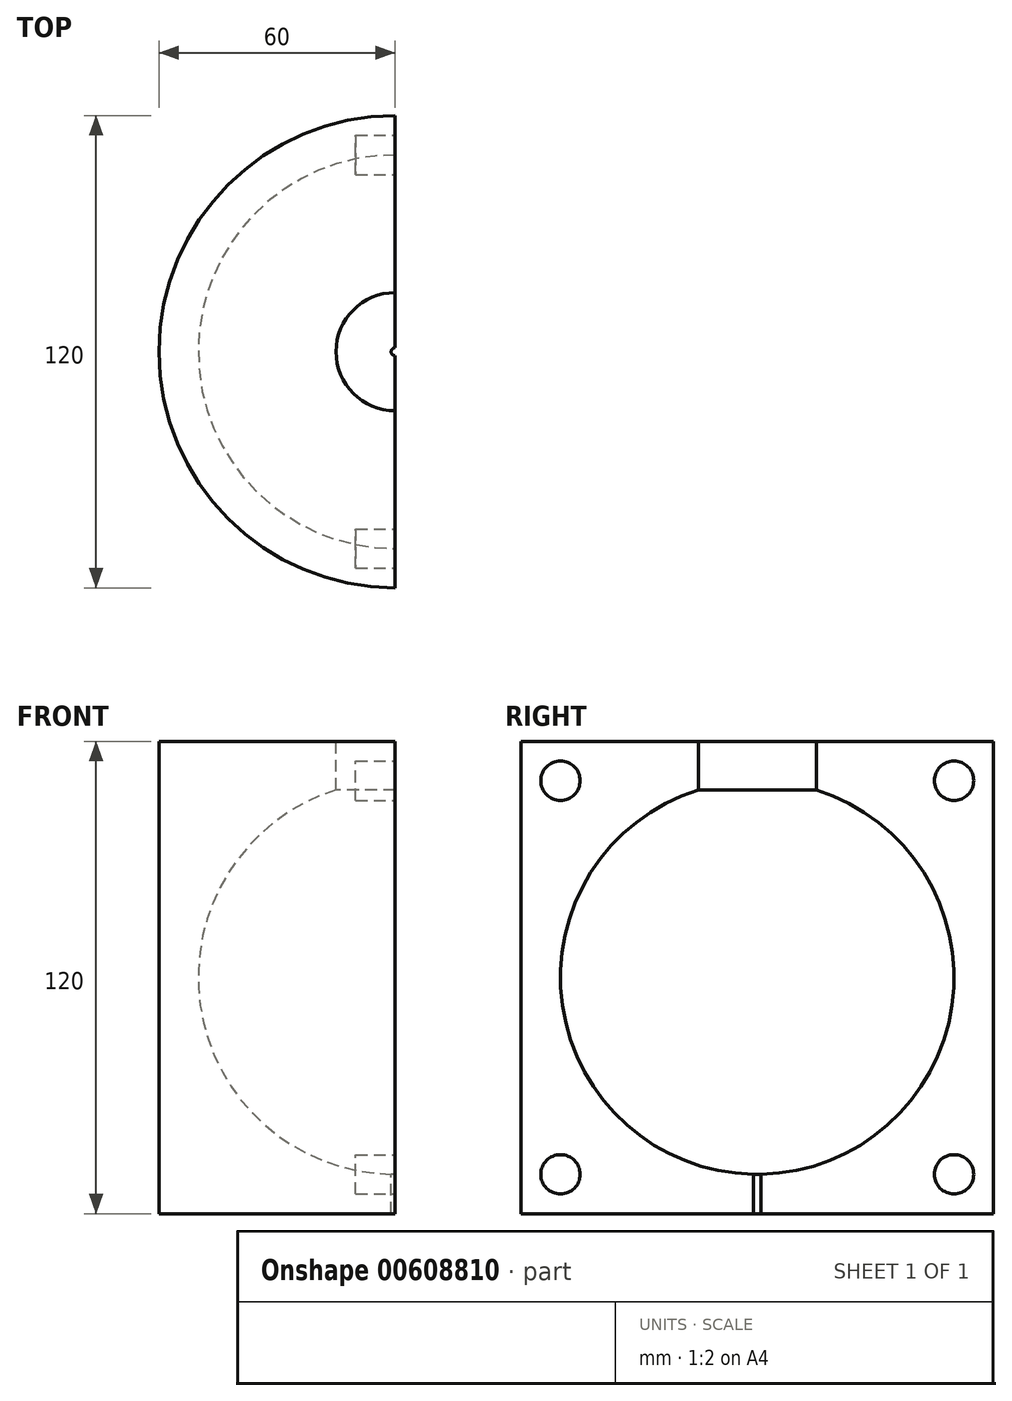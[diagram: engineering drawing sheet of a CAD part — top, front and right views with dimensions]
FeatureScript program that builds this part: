
annotation { "Feature Type Name" : "Feature", "Feature Type Description" : "" }
export const myFeature = defineFeature(function(context is Context, id is Id, definition is map)
    precondition{}
    {
        {
            var Q0;
            Q0=qCreatedBy(makeId("Right.planeOp"),FACE);
            var sketch = newSketch(context, id + "F0", { "sketchPlane" : qUnion([Q0])});
            skLineSegment(sketch, "E0", {"start": v(6.46, -45.64) * mm, "end": v(6.46, 64.36) * mm, "construction": true});
            skLineSegment(sketch, "E1", {"start": v(6.46, 64.36) * mm, "end": v(-8.54, 64.36) * mm, "construction": true});
            skLineSegment(sketch, "E2", {"start": v(-8.54, 64.36) * mm, "end": v(-53.54, 64.36) * mm});
            skLineSegment(sketch, "E3", {"start": v(-53.54, 64.36) * mm, "end": v(-53.54, -55.64) * mm});
            skLineSegment(sketch, "E4", {"start": v(-53.54, -55.64) * mm, "end": v(5.46, -55.64) * mm});
            skLineSegment(sketch, "E5", {"start": v(-8.54, 64.36) * mm, "end": v(-8.54, 54.36) * mm});
            skPoint(sketch, "E6", {"position": v(6.46, 4.36) * mm});
            skLineSegment(sketch, "E7", {"start": v(-8.54, 54.36) * mm, "end": v(-8.54, 52.06) * mm});
            skPoint(sketch, "E8", {"position": v(-43.54, 4.36) * mm});
            skPoint(sketch, "E9", {"position": v(6.46, -45.64) * mm});
            skPoint(sketch, "E10", {"position": v(-8.54, -45.64) * mm});
            skLineSegment(sketch, "E11", {"start": v(-8.54, -45.64) * mm, "end": v(5.46, -45.64) * mm});
            skPoint(sketch, "E12.orphan", {"position": v(-8.54, -55.64) * mm});
            skPoint(sketch, "E13", {"position": v(-43.54, 54.36) * mm});
            skLineSegment(sketch, "E14", {"start": v(-43.54, 4.36) * mm, "end": v(-43.54, 4.36) * mm});
            skArc(sketch, "E15.filletArc", {"start": v(-8.54, 52.06) * mm, "mid": v(-33.85, 33.94) * mm, "end": v(-43.54, 4.36) * mm});
            skPoint(sketch, "E16.visualSharp", {"position": v(-43.54, -45.64) * mm});
            skArc(sketch, "E16.filletArc", {"start": v(-43.54, 4.36) * mm, "mid": v(-28.9, -31) * mm, "end": v(6.46, -45.64) * mm});
            skLineSegment(sketch, "E17", {"start": v(5.46, -45.64) * mm, "end": v(5.46, -55.64) * mm});
            skPoint(sketch, "E18.orphan", {"position": v(6.46, -55.64) * mm});
            skLineSegment(sketch, "E19", {"start": v(5.46, -45.64) * mm, "end": v(5.46, -45.6) * mm});
            skLineSegment(sketch, "E20.MirrorCS", {"start": v(66.46, -55.64) * mm, "end": v(7.46, -55.64) * mm});
            skLineSegment(sketch, "E21.MirrorCS", {"start": v(66.46, 64.36) * mm, "end": v(66.46, -55.64) * mm});
            skLineSegment(sketch, "E22.MirrorCS", {"start": v(21.46, 64.36) * mm, "end": v(66.46, 64.36) * mm});
            skLineSegment(sketch, "E23.MirrorCS", {"start": v(21.46, 64.36) * mm, "end": v(21.46, 54.36) * mm});
            skLineSegment(sketch, "E24.MirrorCS", {"start": v(21.46, 54.36) * mm, "end": v(21.46, 52.06) * mm});
            skArc(sketch, "E25.MirrorCS", {"start": v(21.46, 52.06) * mm, "mid": v(46.77, 33.94) * mm, "end": v(56.46, 4.36) * mm});
            skArc(sketch, "E26.MirrorCS", {"start": v(56.46, 4.36) * mm, "mid": v(41.82, -31) * mm, "end": v(6.46, -45.64) * mm});
            skLineSegment(sketch, "E27.MirrorCS", {"start": v(7.46, -45.64) * mm, "end": v(7.46, -55.64) * mm});
            skLineSegment(sketch, "E28.MirrorCS", {"start": v(7.46, -45.64) * mm, "end": v(7.46, -45.6) * mm});
            skPoint(sketch, "E29.MirrorP", {"position": v(56.46, -45.64) * mm});
            skPoint(sketch, "E30.MirrorP", {"position": v(56.46, 54.36) * mm});
            skCircle(sketch, "E31", {"center": v(-43.54, -45.64) * mm, "radius": 5 * mm});
            skCircle(sketch, "E32", {"center": v(-43.54, 54.36) * mm, "radius": 5 * mm});
            skCircle(sketch, "E33", {"center": v(56.46, -45.64) * mm, "radius": 5 * mm});
            skCircle(sketch, "E34", {"center": v(56.46, 54.36) * mm, "radius": 5 * mm});
            skSolve(sketch);
        }
        {
            var Q0;
            Q0=makeQuery(id+"F0.imprint","IMPRINT",FACE,{"disambiguationData":[TD([[makeQuery(id+"F0.imprint","IMPRINT",EDGE,{"derivedFrom":sQuery(id+"F0.wireOp",EDGE,"E2")}),1.0]])]});
            var Q1;
            Q1=makeQuery(id+"F0.imprint","IMPRINT",FACE,{"disambiguationData":[TD([[makeQuery(id+"F0.imprint","IMPRINT",EDGE,{"derivedFrom":sQuery(id+"F0.wireOp",EDGE,"E32")}),1.0]])]});
            var Q2;
            Q2=makeQuery(id+"F0.imprint","IMPRINT",FACE,{"disambiguationData":[TD([[makeQuery(id+"F0.imprint","IMPRINT",EDGE,{"derivedFrom":sQuery(id+"F0.wireOp",EDGE,"E31")}),1.0]])]});
            var Q3;
            Q3=sQuery(id+"F0.wireOp",EDGE,"E0");
            revolve(context, id + "F1", {"entities" : qUnion([Q0, Q1, Q2]), "axis" : qUnion([Q3]), "revolveType" : RevolveType.ONE_DIRECTION, "oppositeDirection" : true, "angle" : 180 * degree});
        }
        {
            var Q0;
            Q0=makeQuery(id+"F0.imprint","IMPRINT",FACE,{"disambiguationData":[TD([[makeQuery(id+"F0.imprint","IMPRINT",EDGE,{"derivedFrom":sQuery(id+"F0.wireOp",EDGE,"E32")}),1.0]])]});
            var Q1;
            Q1=makeQuery(id+"F0.imprint","IMPRINT",FACE,{"disambiguationData":[TD([[makeQuery(id+"F0.imprint","IMPRINT",EDGE,{"derivedFrom":sQuery(id+"F0.wireOp",EDGE,"E34")}),1.0]])]});
            var Q2;
            Q2=makeQuery(id+"F0.imprint","IMPRINT",FACE,{"disambiguationData":[TD([[makeQuery(id+"F0.imprint","IMPRINT",EDGE,{"derivedFrom":sQuery(id+"F0.wireOp",EDGE,"E31")}),1.0]])]});
            var Q3;
            Q3=makeQuery(id+"F0.imprint","IMPRINT",FACE,{"disambiguationData":[TD([[makeQuery(id+"F0.imprint","IMPRINT",EDGE,{"derivedFrom":sQuery(id+"F0.wireOp",EDGE,"E33")}),1.0]])]});
            var Q4;
            Q4=sQuery(id+"F0.wireOp",EDGE,"E32");
            var Q5;
            Q5=sQuery(id+"F0.wireOp",EDGE,"E34");
            var Q6;
            Q6=sQuery(id+"F0.wireOp",EDGE,"E31");
            var Q7;
            Q7=sQuery(id+"F0.wireOp",EDGE,"E33");
            extrude(context, id + "F2", {"entities" : qUnion([Q0, Q1, Q2, Q3]), "operationType" : NewBodyOperationType.REMOVE, "surfaceEntities" : qUnion([Q4, Q5, Q6, Q7]), "oppositeDirection" : true, "depth" : 10 * mm, "offsetDistance" : 25 * mm});
        }
    });
